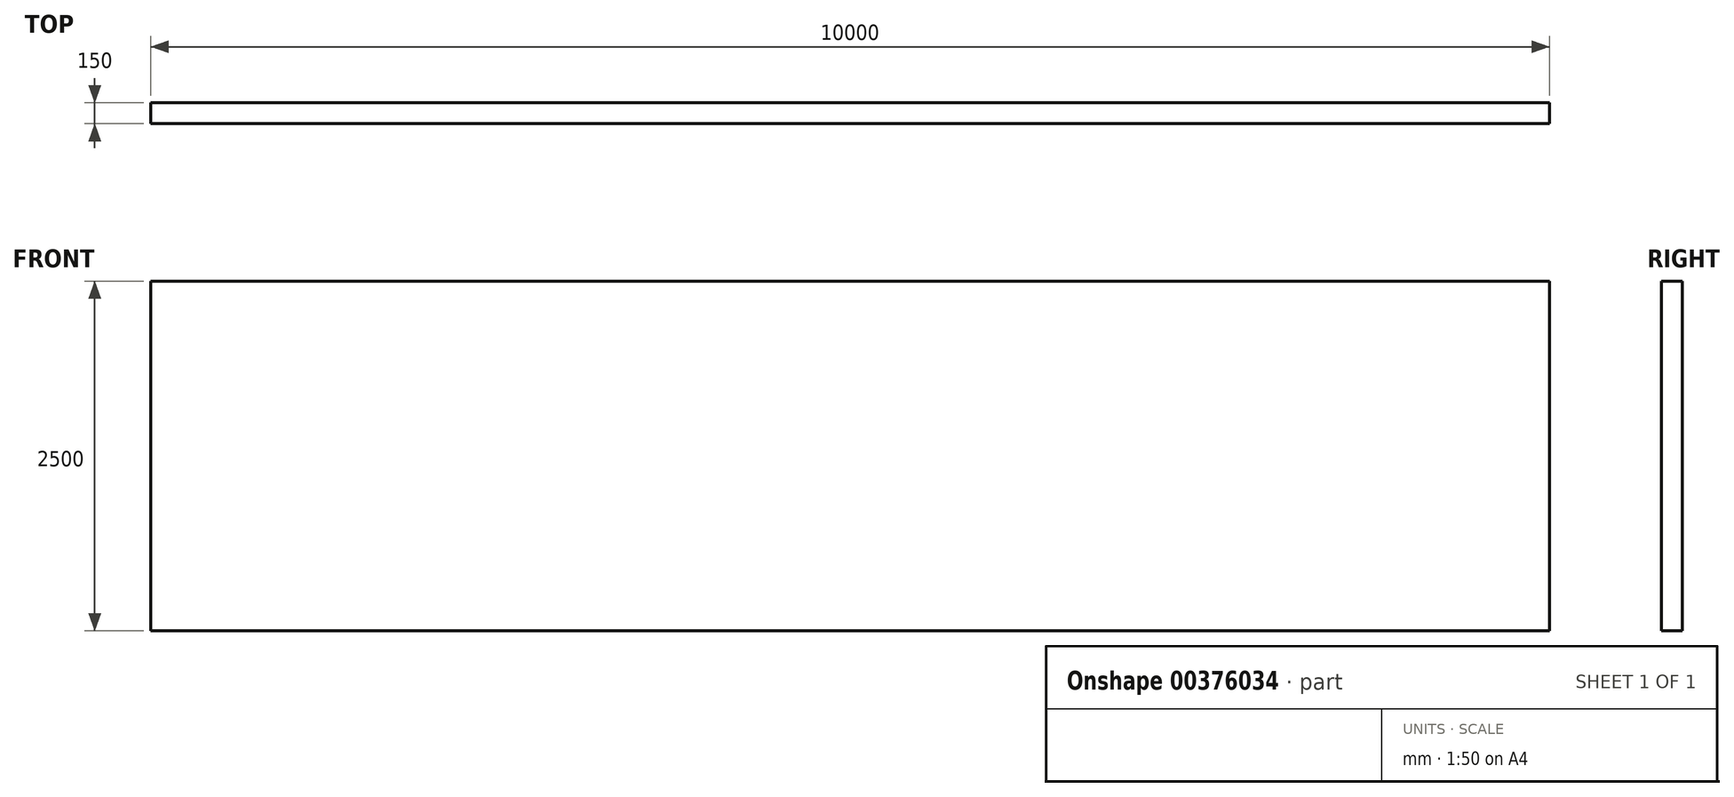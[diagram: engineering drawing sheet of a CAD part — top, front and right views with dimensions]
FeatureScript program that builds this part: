
annotation { "Feature Type Name" : "Feature", "Feature Type Description" : "" }
export const myFeature = defineFeature(function(context is Context, id is Id, definition is map)
    precondition{}
    {
        {
            var Q0;
            Q0=qCreatedBy(makeId("Top.planeOp"),FACE);
            var sketch = newSketch(context, id + "F0", { "sketchPlane" : qUnion([Q0])});
            skLineSegment(sketch, "E0.bottom", {"start": v(-4991.52, -637.3) * mm, "end": v(5008.48, -637.3) * mm});
            skLineSegment(sketch, "E0.top", {"start": v(-4991.52, -487.3) * mm, "end": v(5008.48, -487.3) * mm});
            skLineSegment(sketch, "E0.left", {"start": v(-4991.52, -637.3) * mm, "end": v(-4991.52, -487.3) * mm});
            skLineSegment(sketch, "E0.right", {"start": v(5008.48, -637.3) * mm, "end": v(5008.48, -487.3) * mm});
            skSolve(sketch);
        }
        {
            var Q0;
            Q0=makeQuery(id+"F0.imprint","IMPRINT",FACE,{"disambiguationData":[TD([[makeQuery(id+"F0.imprint","IMPRINT",EDGE,{"derivedFrom":sQuery(id+"F0.wireOp",EDGE,"E0.bottom")}),1.0]])]});
            extrude(context, id + "F1", {"entities" : qUnion([Q0]), "depth" : 2500 * mm});
        }
    });
